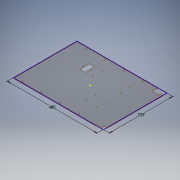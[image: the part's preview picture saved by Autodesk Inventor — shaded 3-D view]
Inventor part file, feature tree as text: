
AUTODESK INVENTOR PART (.ipt)
format: ipt  version: 2019.4 (Build 234330000, 330)  size: 210,432 bytes
history: native  units: mm
features: sketch x6, extrude x5
ambient origin geometry x8: Origin, YZ Plane, XZ Plane, XY Plane, X Axis, Y Axis, Z Axis, Center Point
bodies: Solid1 (feature_tree)
feature tree (11):
  extrude  "Extrusion1"  Depth=337.83mm
  extrude  "Extrusion2"  Depth=20.0mm
  extrude  "Extrusion3"  Depth=8.0mm
  sketch  "Sketch5"  dims[d7=90.0deg d8=12.0mm]
  extrude  "Extrusion4"  Depth=12.0mm
  extrude  "Extrusion5"  Depth=5.0mm TaperAngle=0.0deg
  sketch  "Sketch1"  dims[d0=480.0mm d1=337.83mm]
  sketch  "Sketch2"  dims[d2=5.0mm d3=0.0mm d4=20.0mm]
  sketch  "Sketch4"  dims[d5=15.0mm d6=8.0mm]
  sketch  "Sketch8"  dims[d9=32.0mm d10=5.0mm d11=0.0mm]
  sketch  "Sketch9"  dims[d14=40.0mm d15=8.732mm d16=5.5mm d17=40.0mm d19=100.0mm d20=10.0mm d22=10.0mm d24=60.0mm d25=8.732mm d26=5.5mm d27=40.0mm d29=100.0mm d30=10.0mm d32=10.0mm d34=10.0mm d35=0.0mm d36=480.0mm d37=339.0mm d38=35.0mm d39=20.0mm d40=10.0mm d41=0.0mm d42=4.0mm d43=70.0mm d44=125.0mm d45=20.0mm d47=50.0mm d48=20.0mm d50=150.0mm d53=40.0mm d54=180.0deg d55=15.0mm d56=15.0mm d57=29.0mm d58=50.0mm d59=5.5mm d60=5.5mm d61=3.5mm d62=3.5mm d63=3.5mm d64=90.0mm d65=125.0mm d66=20.0mm d68=58.0mm d69=20.0mm d71=49.0mm d74=10.0mm d75=0.0mm]
